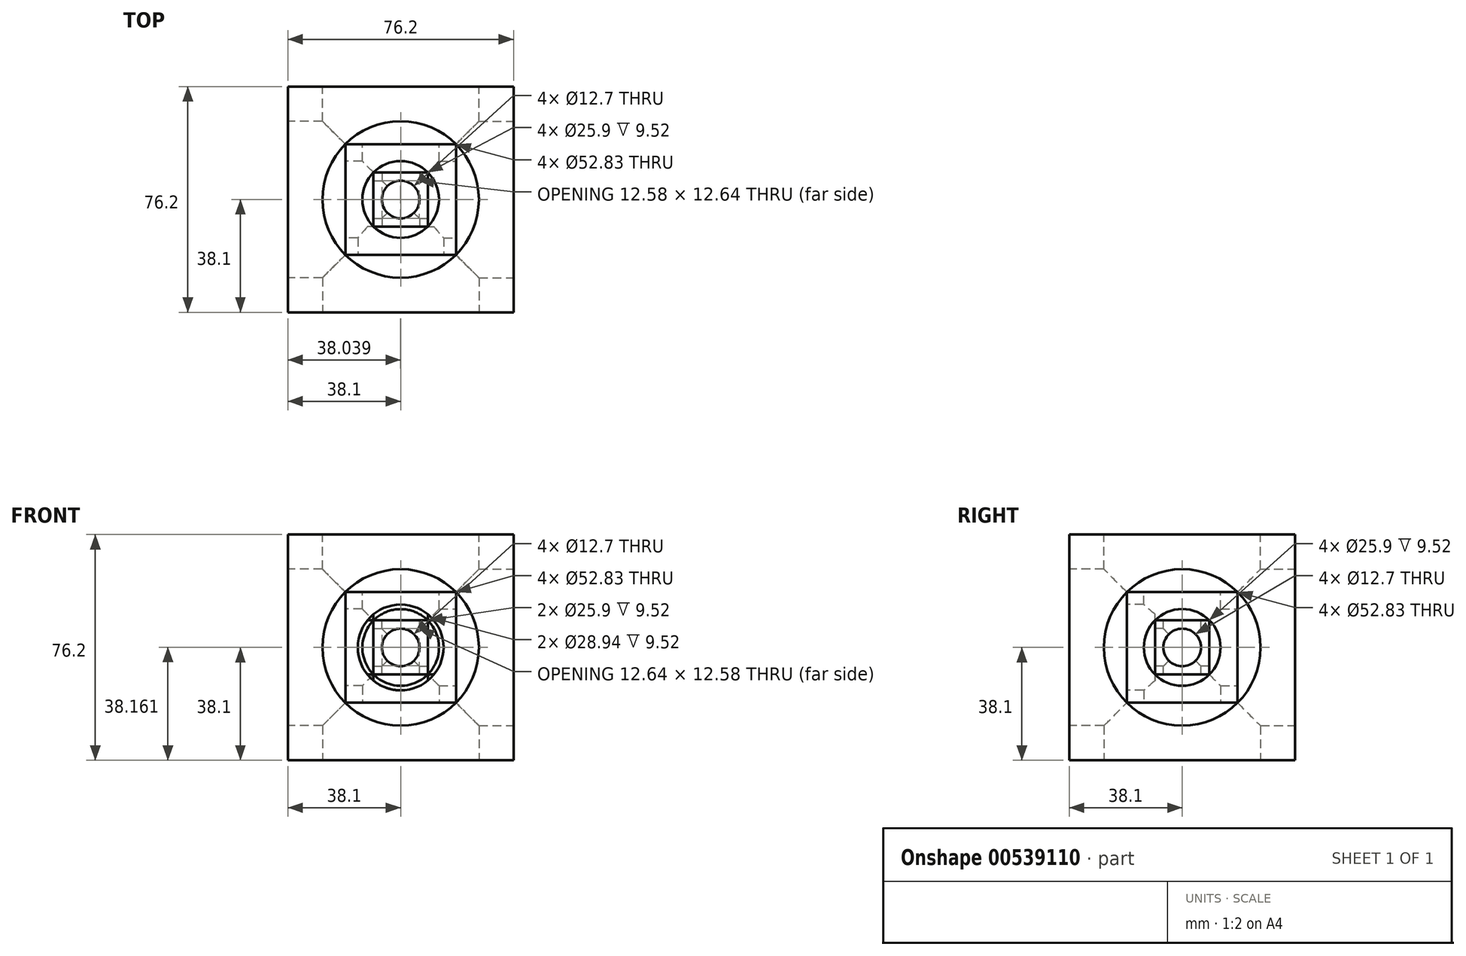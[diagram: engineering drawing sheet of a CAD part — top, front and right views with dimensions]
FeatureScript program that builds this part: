
annotation { "Feature Type Name" : "Feature", "Feature Type Description" : "" }
export const myFeature = defineFeature(function(context is Context, id is Id, definition is map)
    precondition{}
    {
        {
            var Q0;
            Q0=qCreatedBy(makeId("Front.planeOp"),FACE);
            var sketch = newSketch(context, id + "F0", { "sketchPlane" : qUnion([Q0])});
            skLineSegment(sketch, "E0.bottom", {"start": v(-38.1, 38.1) * mm, "end": v(38.1, 38.1) * mm});
            skLineSegment(sketch, "E0.top", {"start": v(-38.1, -38.1) * mm, "end": v(38.1, -38.1) * mm});
            skLineSegment(sketch, "E0.left", {"start": v(-38.1, 38.1) * mm, "end": v(-38.1, -38.1) * mm});
            skLineSegment(sketch, "E0.right", {"start": v(38.1, 38.1) * mm, "end": v(38.1, -38.1) * mm});
            skSolve(sketch);
        }
        {
            var Q0;
            Q0 = qSketchRegion(id + "F0", true);
            extrude(context, id + "F1", {"entities" : qUnion([Q0]), "depth" : 38.1 * mm, "offsetDistance" : 25.4 * mm, "hasSecondDirection" : true, "secondDirectionOppositeDirection" : true, "secondDirectionDepth" : 38.1 * mm});
        }
        {
            var Q0;
            Q0=makeQuery(id+"F1.opExtrude","CAP_FACE",FACE,{"disambiguationData":[OSD([sQuery(id+"F0.wireOp",EDGE,"E0.bottom"),sQuery(id+"F0.wireOp",EDGE,"E0.top"),sQuery(id+"F0.wireOp",EDGE,"E0.left"),sQuery(id+"F0.wireOp",EDGE,"E0.right")])],"isStart":false});
            var sketch = newSketch(context, id + "F2", { "sketchPlane" : qUnion([Q0])});
            skCircle(sketch, "E1", {"center": v(0, 0) * mm, "radius": 6.35 * mm});
            skSolve(sketch);
        }
        {
            var Q0;
            Q0 = qSketchRegion(id + "F2", true);
            extrude(context, id + "F3", {"entities" : qUnion([Q0]), "operationType" : NewBodyOperationType.REMOVE, "endBound" : BoundingType.THROUGH_ALL, "oppositeDirection" : true, "depth" : 25.4 * mm, "offsetDistance" : 25.4 * mm});
        }
        {
            var Q0;
            Q0=makeQuery(id+"F1.opExtrude","SWEPT_FACE",FACE,{"disambiguationData":[OSD([sQuery(id+"F0.wireOp",EDGE,"E0.bottom")])]});
            var sketch = newSketch(context, id + "F4", { "sketchPlane" : qUnion([Q0])});
            skCircle(sketch, "E2", {"center": v(0, 0) * mm, "radius": 6.35 * mm});
            skSolve(sketch);
        }
        {
            var Q0;
            Q0=makeQuery(id+"F4.imprint","IMPRINT",FACE,{"disambiguationData":[TD([[makeQuery(id+"F4.imprint","IMPRINT",EDGE,{"derivedFrom":sQuery(id+"F4.wireOp",EDGE,"E2")}),1.0]])]});
            extrude(context, id + "F5", {"entities" : qUnion([Q0]), "operationType" : NewBodyOperationType.REMOVE, "endBound" : BoundingType.THROUGH_ALL, "oppositeDirection" : true, "depth" : 25.4 * mm, "offsetDistance" : 25.4 * mm});
        }
        {
            var Q0;
            Q0=makeQuery(id+"F1.opExtrude","SWEPT_FACE",FACE,{"disambiguationData":[OSD([sQuery(id+"F0.wireOp",EDGE,"E0.right")])]});
            var sketch = newSketch(context, id + "F6", { "sketchPlane" : qUnion([Q0])});
            skCircle(sketch, "E3", {"center": v(0, 0) * mm, "radius": 6.35 * mm});
            skSolve(sketch);
        }
        {
            var Q0;
            Q0=makeQuery(id+"F6.imprint","IMPRINT",FACE,{"disambiguationData":[TD([[makeQuery(id+"F6.imprint","IMPRINT",EDGE,{"derivedFrom":sQuery(id+"F6.wireOp",EDGE,"E3")}),1.0]])]});
            extrude(context, id + "F7", {"entities" : qUnion([Q0]), "operationType" : NewBodyOperationType.REMOVE, "endBound" : BoundingType.THROUGH_ALL, "oppositeDirection" : true, "depth" : 25.4 * mm, "offsetDistance" : 25.4 * mm});
        }
        {
            var Q0;
            Q0=makeQuery(id+"F1.opExtrude","SWEPT_FACE",FACE,{"disambiguationData":[OSD([sQuery(id+"F0.wireOp",EDGE,"E0.left")])]});
            var sketch = newSketch(context, id + "F8", { "sketchPlane" : qUnion([Q0])});
            skCircle(sketch, "E4", {"center": v(0, 0) * mm, "radius": 26.42 * mm});
            skSolve(sketch);
        }
        {
            var Q0;
            Q0=makeQuery(id+"F8.imprint","IMPRINT",FACE,{"disambiguationData":[TD([[makeQuery(id+"F8.imprint","IMPRINT",EDGE,{"derivedFrom":sQuery(id+"F8.wireOp",EDGE,"E4")}),-1.0]])]});
            var sketch = newSketch(context, id + "F9", { "sketchPlane" : qUnion([Q0])});
            skCircle(sketch, "E5", {"center": v(0, 0) * mm, "radius": 12.95 * mm});
            skSolve(sketch);
        }
        {
            var Q0;
            Q0 = qSketchRegion(id + "F9", true);
            var Q1;
            Q1=makeQuery(id+"F8.imprint","IMPRINT",FACE,{"disambiguationData":[TD([[makeQuery(id+"F8.imprint","IMPRINT",EDGE,{"derivedFrom":sQuery(id+"F8.wireOp",EDGE,"E4")}),1.0]])]});
            extrude(context, id + "F10", {"entities" : qUnion([Q0, Q1]), "operationType" : NewBodyOperationType.REMOVE, "oppositeDirection" : true, "depth" : 19.42 * mm, "offsetDistance" : 25.4 * mm});
        }
        {
            var Q0;
            Q0 = qSketchRegion(id + "F9", true);
            extrude(context, id + "F11", {"entities" : qUnion([Q0]), "operationType" : NewBodyOperationType.REMOVE, "oppositeDirection" : true, "depth" : 28.94 * mm, "offsetDistance" : 25.4 * mm});
        }
        {
            var Q0;
            Q0=makeQuery(id+"F1.opExtrude","SWEPT_FACE",FACE,{"disambiguationData":[OSD([sQuery(id+"F0.wireOp",EDGE,"E0.bottom")])]});
            var sketch = newSketch(context, id + "F12", { "sketchPlane" : qUnion([Q0])});
            skCircle(sketch, "E6", {"center": v(0, 0) * mm, "radius": 26.42 * mm});
            skSolve(sketch);
        }
        {
            var Q0;
            Q0=makeQuery(id+"F12.imprint","IMPRINT",FACE,{"disambiguationData":[TD([[makeQuery(id+"F12.imprint","IMPRINT",EDGE,{"derivedFrom":sQuery(id+"F12.wireOp",EDGE,"E6")}),-1.0]])]});
            var sketch = newSketch(context, id + "F13", { "sketchPlane" : qUnion([Q0])});
            skCircle(sketch, "E7", {"center": v(0, 0) * mm, "radius": 12.95 * mm});
            skSolve(sketch);
        }
        {
            var Q0;
            Q0=makeQuery(id+"F12.imprint","IMPRINT",FACE,{"disambiguationData":[TD([[makeQuery(id+"F12.imprint","IMPRINT",EDGE,{"derivedFrom":sQuery(id+"F12.wireOp",EDGE,"E6")}),1.0]])]});
            extrude(context, id + "F14", {"entities" : qUnion([Q0]), "operationType" : NewBodyOperationType.REMOVE, "oppositeDirection" : true, "depth" : 19.42 * mm, "offsetDistance" : 25.4 * mm});
        }
        {
            var Q0;
            Q0=makeQuery(id+"F13.imprint","IMPRINT",FACE,{"disambiguationData":[TD([[makeQuery(id+"F13.imprint","IMPRINT",EDGE,{"derivedFrom":sQuery(id+"F13.wireOp",EDGE,"E7")}),1.0]])]});
            extrude(context, id + "F15", {"entities" : qUnion([Q0]), "operationType" : NewBodyOperationType.REMOVE, "oppositeDirection" : true, "depth" : 28.94 * mm, "offsetDistance" : 25.4 * mm});
        }
        {
            var Q0;
            Q0=makeQuery(id+"F1.opExtrude","CAP_FACE",FACE,{"disambiguationData":[OSD([sQuery(id+"F0.wireOp",EDGE,"E0.bottom"),sQuery(id+"F0.wireOp",EDGE,"E0.top"),sQuery(id+"F0.wireOp",EDGE,"E0.left"),sQuery(id+"F0.wireOp",EDGE,"E0.right")])],"isStart":true});
            var sketch = newSketch(context, id + "F16", { "sketchPlane" : qUnion([Q0])});
            skCircle(sketch, "E8", {"center": v(0, 0) * mm, "radius": 26.42 * mm});
            skSolve(sketch);
        }
        {
            var Q0;
            Q0=makeQuery(id+"F16.imprint","IMPRINT",FACE,{"disambiguationData":[TD([[makeQuery(id+"F16.imprint","IMPRINT",EDGE,{"derivedFrom":sQuery(id+"F16.wireOp",EDGE,"E8")}),-1.0]])]});
            var sketch = newSketch(context, id + "F17", { "sketchPlane" : qUnion([Q0])});
            skCircle(sketch, "E9", {"center": v(0, 0) * mm, "radius": 12.95 * mm});
            skSolve(sketch);
        }
        {
            var Q0;
            Q0=makeQuery(id+"F16.imprint","IMPRINT",FACE,{"disambiguationData":[TD([[makeQuery(id+"F16.imprint","IMPRINT",EDGE,{"derivedFrom":sQuery(id+"F16.wireOp",EDGE,"E8")}),1.0]])]});
            extrude(context, id + "F18", {"entities" : qUnion([Q0]), "operationType" : NewBodyOperationType.REMOVE, "oppositeDirection" : true, "depth" : 19.42 * mm, "offsetDistance" : 25.4 * mm});
        }
        {
            var Q0;
            Q0=makeQuery(id+"F17.imprint","IMPRINT",FACE,{"disambiguationData":[TD([[makeQuery(id+"F17.imprint","IMPRINT",EDGE,{"derivedFrom":sQuery(id+"F17.wireOp",EDGE,"E9")}),1.0]])]});
            extrude(context, id + "F19", {"entities" : qUnion([Q0]), "operationType" : NewBodyOperationType.REMOVE, "oppositeDirection" : true, "depth" : 28.94 * mm, "offsetDistance" : 25.4 * mm});
        }
        {
            var Q0;
            Q0=makeQuery(id+"F1.opExtrude","SWEPT_FACE",FACE,{"disambiguationData":[OSD([sQuery(id+"F0.wireOp",EDGE,"E0.right")])]});
            var sketch = newSketch(context, id + "F20", { "sketchPlane" : qUnion([Q0])});
            skCircle(sketch, "E10", {"center": v(0, 0) * mm, "radius": 26.42 * mm});
            skSolve(sketch);
        }
        {
            var Q0;
            Q0=makeQuery(id+"F20.imprint","IMPRINT",FACE,{"disambiguationData":[TD([[makeQuery(id+"F20.imprint","IMPRINT",EDGE,{"derivedFrom":sQuery(id+"F20.wireOp",EDGE,"E10")}),-1.0]])]});
            var sketch = newSketch(context, id + "F21", { "sketchPlane" : qUnion([Q0])});
            skCircle(sketch, "E11", {"center": v(0, 0) * mm, "radius": 12.95 * mm});
            skSolve(sketch);
        }
        {
            var Q0;
            Q0=makeQuery(id+"F20.imprint","IMPRINT",FACE,{"disambiguationData":[TD([[makeQuery(id+"F20.imprint","IMPRINT",EDGE,{"derivedFrom":sQuery(id+"F20.wireOp",EDGE,"E10")}),1.0]])]});
            extrude(context, id + "F22", {"entities" : qUnion([Q0]), "operationType" : NewBodyOperationType.REMOVE, "oppositeDirection" : true, "depth" : 19.42 * mm, "offsetDistance" : 25.4 * mm});
        }
        {
            var Q0;
            Q0=makeQuery(id+"F21.imprint","IMPRINT",FACE,{"disambiguationData":[TD([[makeQuery(id+"F21.imprint","IMPRINT",EDGE,{"derivedFrom":sQuery(id+"F21.wireOp",EDGE,"E11")}),1.0]])]});
            extrude(context, id + "F23", {"entities" : qUnion([Q0]), "operationType" : NewBodyOperationType.REMOVE, "oppositeDirection" : true, "depth" : 28.94 * mm, "offsetDistance" : 25.4 * mm});
        }
        {
            var Q0;
            Q0=makeQuery(id+"F1.opExtrude","CAP_FACE",FACE,{"disambiguationData":[OSD([sQuery(id+"F0.wireOp",EDGE,"E0.bottom"),sQuery(id+"F0.wireOp",EDGE,"E0.top"),sQuery(id+"F0.wireOp",EDGE,"E0.left"),sQuery(id+"F0.wireOp",EDGE,"E0.right")])],"isStart":false});
            var sketch = newSketch(context, id + "F24", { "sketchPlane" : qUnion([Q0])});
            skCircle(sketch, "E12", {"center": v(0, 0) * mm, "radius": 26.42 * mm});
            skSolve(sketch);
        }
        {
            var Q0;
            Q0=makeQuery(id+"F24.imprint","IMPRINT",FACE,{"disambiguationData":[TD([[makeQuery(id+"F24.imprint","IMPRINT",EDGE,{"derivedFrom":sQuery(id+"F24.wireOp",EDGE,"E12")}),-1.0]])]});
            var sketch = newSketch(context, id + "F25", { "sketchPlane" : qUnion([Q0])});
            skCircle(sketch, "E13", {"center": v(0, 0) * mm, "radius": 14.47 * mm});
            skSolve(sketch);
        }
        {
            var Q0;
            Q0=makeQuery(id+"F24.imprint","IMPRINT",FACE,{"disambiguationData":[TD([[makeQuery(id+"F24.imprint","IMPRINT",EDGE,{"derivedFrom":sQuery(id+"F24.wireOp",EDGE,"E12")}),1.0]])]});
            extrude(context, id + "F26", {"entities" : qUnion([Q0]), "operationType" : NewBodyOperationType.REMOVE, "oppositeDirection" : true, "depth" : 19.42 * mm, "offsetDistance" : 25.4 * mm});
        }
        {
            var Q0;
            Q0=makeQuery(id+"F25.imprint","IMPRINT",FACE,{"disambiguationData":[TD([[makeQuery(id+"F25.imprint","IMPRINT",EDGE,{"derivedFrom":sQuery(id+"F25.wireOp",EDGE,"E13")}),1.0]])]});
            extrude(context, id + "F27", {"entities" : qUnion([Q0]), "operationType" : NewBodyOperationType.REMOVE, "oppositeDirection" : true, "depth" : 28.94 * mm, "offsetDistance" : 25.4 * mm});
        }
        {
            var Q0;
            Q0=makeQuery(id+"F1.opExtrude","SWEPT_FACE",FACE,{"disambiguationData":[OSD([sQuery(id+"F0.wireOp",EDGE,"E0.top")])]});
            var sketch = newSketch(context, id + "F28", { "sketchPlane" : qUnion([Q0])});
            skCircle(sketch, "E14", {"center": v(0, 0) * mm, "radius": 26.42 * mm});
            skSolve(sketch);
        }
        {
            var Q0;
            Q0=makeQuery(id+"F28.imprint","IMPRINT",FACE,{"disambiguationData":[TD([[makeQuery(id+"F28.imprint","IMPRINT",EDGE,{"derivedFrom":sQuery(id+"F28.wireOp",EDGE,"E14")}),-1.0]])]});
            var sketch = newSketch(context, id + "F29", { "sketchPlane" : qUnion([Q0])});
            skCircle(sketch, "E15", {"center": v(0, 0) * mm, "radius": 12.95 * mm});
            skSolve(sketch);
        }
        {
            var Q0;
            Q0=makeQuery(id+"F28.imprint","IMPRINT",FACE,{"disambiguationData":[TD([[makeQuery(id+"F28.imprint","IMPRINT",EDGE,{"derivedFrom":sQuery(id+"F28.wireOp",EDGE,"E14")}),1.0]])]});
            extrude(context, id + "F30", {"entities" : qUnion([Q0]), "operationType" : NewBodyOperationType.REMOVE, "oppositeDirection" : true, "depth" : 19.42 * mm, "offsetDistance" : 25.4 * mm});
        }
        {
            var Q0;
            Q0=makeQuery(id+"F29.imprint","IMPRINT",FACE,{"disambiguationData":[TD([[makeQuery(id+"F29.imprint","IMPRINT",EDGE,{"derivedFrom":sQuery(id+"F29.wireOp",EDGE,"E15")}),1.0]])]});
            extrude(context, id + "F31", {"entities" : qUnion([Q0]), "operationType" : NewBodyOperationType.REMOVE, "oppositeDirection" : true, "depth" : 28.94 * mm, "offsetDistance" : 25.4 * mm});
        }
    });
